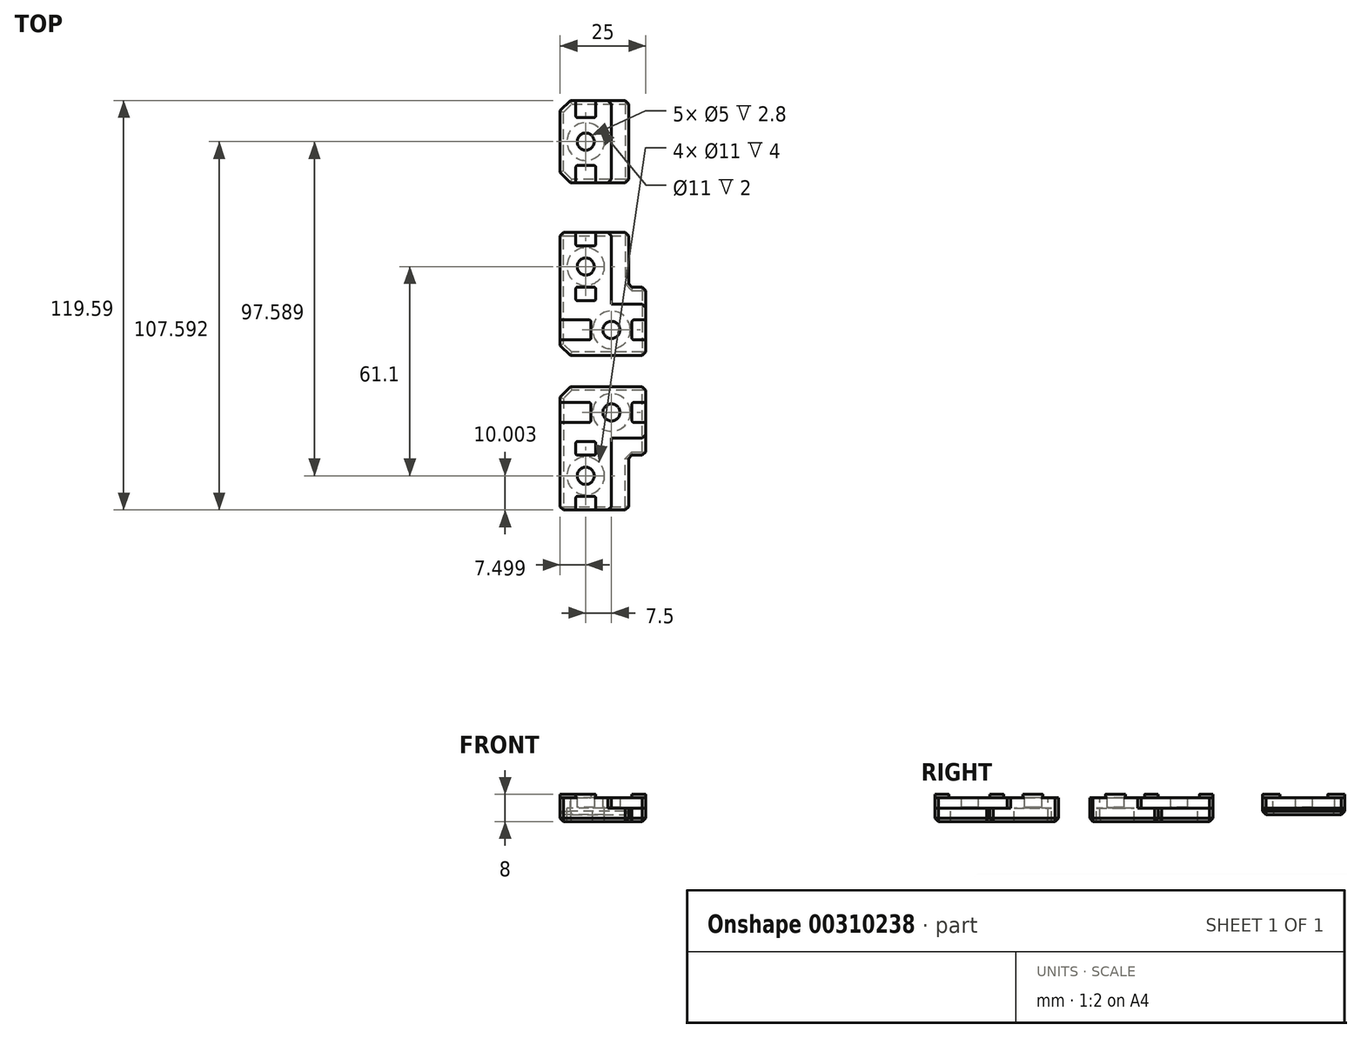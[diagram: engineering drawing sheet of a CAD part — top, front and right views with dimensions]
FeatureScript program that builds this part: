
annotation { "Feature Type Name" : "Feature", "Feature Type Description" : "" }
export const myFeature = defineFeature(function(context is Context, id is Id, definition is map)
    precondition{}
    {
        {
            var Q0;
            Q0=qCreatedBy(makeId("Top.planeOp"),FACE);
            var sketch = newSketch(context, id + "F0", { "sketchPlane" : qUnion([Q0])});
            skLineSegment(sketch, "E0", {"start": v(-211.12, 45.44) * mm, "end": v(-211.12, 81.44) * mm});
            skLineSegment(sketch, "E1", {"start": v(-211.12, 45.44) * mm, "end": v(-186.12, 45.44) * mm});
            skLineSegment(sketch, "E2", {"start": v(-211.12, 81.44) * mm, "end": v(-196.12, 81.44) * mm});
            skLineSegment(sketch, "E3", {"start": v(-196.12, 81.44) * mm, "end": v(-196.12, 60.44) * mm});
            skLineSegment(sketch, "E4", {"start": v(-196.12, 60.44) * mm, "end": v(-186.12, 60.44) * mm});
            skLineSegment(sketch, "E5", {"start": v(-186.12, 60.44) * mm, "end": v(-186.12, 45.44) * mm});
            skCircle(sketch, "E6", {"center": v(-203.62, 71.44) * mm, "radius": 2.5 * mm});
            skPoint(sketch, "E6.centerSnap0", {"position": v(-203.62, 81.44) * mm});
            skCircle(sketch, "E7", {"center": v(-196.12, 52.94) * mm, "radius": 2.5 * mm});
            skPoint(sketch, "E7.centerSnap0", {"position": v(-186.12, 52.94) * mm});
            skLineSegment(sketch, "E8", {"start": v(-191.45, 50.04) * mm, "end": v(-186.12, 50.04) * mm});
            skLineSegment(sketch, "E9", {"start": v(-191.45, 55.84) * mm, "end": v(-186.12, 55.84) * mm});
            skLineSegment(sketch, "E10", {"start": v(-206.52, 76.12) * mm, "end": v(-206.52, 81.44) * mm});
            skLineSegment(sketch, "E11", {"start": v(-200.72, 76.12) * mm, "end": v(-200.72, 81.44) * mm});
            skLineSegment(sketch, "E12", {"start": v(-200.72, 61.44) * mm, "end": v(-200.72, 66.77) * mm});
            skLineSegment(sketch, "E13", {"start": v(-206.52, 66.77) * mm, "end": v(-206.52, 61.44) * mm});
            skCircle(sketch, "E14", {"center": v(-203.62, 71.44) * mm, "radius": 5.5 * mm});
            skCircle(sketch, "E15", {"center": v(-196.12, 52.94) * mm, "radius": 5.5 * mm});
            skLineSegment(sketch, "E16", {"start": v(-200.8, 55.84) * mm, "end": v(-211.12, 55.84) * mm});
            skLineSegment(sketch, "E17", {"start": v(-200.8, 50.04) * mm, "end": v(-211.12, 50.04) * mm});
            skLineSegment(sketch, "E18", {"start": v(-200.72, 61.44) * mm, "end": v(-206.52, 61.44) * mm});
            skLineSegment(sketch, "E19", {"start": v(-206.52, 77.44) * mm, "end": v(-200.72, 77.44) * mm});
            skLineSegment(sketch, "E20", {"start": v(-200.72, 65.44) * mm, "end": v(-206.52, 65.44) * mm});
            skLineSegment(sketch, "E21", {"start": v(-202.12, 55.84) * mm, "end": v(-202.12, 50.04) * mm});
            skLineSegment(sketch, "E22", {"start": v(-190.12, 50.04) * mm, "end": v(-190.12, 55.84) * mm});
            skLineSegment(sketch, "E23", {"start": v(-186.12, 45.44) * mm, "end": v(-183.12, 45.44) * mm});
            skLineSegment(sketch, "E24", {"start": v(-183.12, 45.44) * mm, "end": v(-183.12, 65.44) * mm});
            skLineSegment(sketch, "E25", {"start": v(-183.12, 65.44) * mm, "end": v(-191.12, 65.44) * mm});
            skLineSegment(sketch, "E26", {"start": v(-191.12, 65.44) * mm, "end": v(-191.12, 84.44) * mm});
            skLineSegment(sketch, "E27", {"start": v(-191.12, 84.44) * mm, "end": v(-211.12, 84.44) * mm});
            skLineSegment(sketch, "E28", {"start": v(-211.12, 84.44) * mm, "end": v(-211.12, 81.44) * mm});
            skLineSegment(sketch, "E29", {"start": v(-211.12, 95.93) * mm, "end": v(-196.12, 95.93) * mm});
            skLineSegment(sketch, "E30", {"start": v(-196.12, 95.93) * mm, "end": v(-196.12, 119.93) * mm});
            skLineSegment(sketch, "E31", {"start": v(-196.12, 119.93) * mm, "end": v(-211.12, 119.93) * mm});
            skLineSegment(sketch, "E32", {"start": v(-211.12, 119.93) * mm, "end": v(-211.12, 95.93) * mm});
            skLineSegment(sketch, "E33", {"start": v(-206.52, 95.93) * mm, "end": v(-206.52, 100.93) * mm});
            skLineSegment(sketch, "E34", {"start": v(-206.52, 100.93) * mm, "end": v(-200.72, 100.93) * mm});
            skLineSegment(sketch, "E35", {"start": v(-200.72, 100.93) * mm, "end": v(-200.72, 95.93) * mm});
            skLineSegment(sketch, "E36", {"start": v(-206.52, 119.93) * mm, "end": v(-206.52, 114.93) * mm});
            skLineSegment(sketch, "E37", {"start": v(-206.52, 114.93) * mm, "end": v(-200.72, 114.93) * mm});
            skLineSegment(sketch, "E38", {"start": v(-200.72, 114.93) * mm, "end": v(-200.72, 119.93) * mm});
            skCircle(sketch, "E39", {"center": v(-203.62, 107.93) * mm, "radius": 5.5 * mm});
            skPoint(sketch, "E39.centerSnap0", {"position": v(-196.12, 107.93) * mm});
            skPoint(sketch, "E39.centerSnap1", {"position": v(-203.62, 100.93) * mm});
            skLineSegment(sketch, "E40", {"start": v(-196.12, 119.93) * mm, "end": v(-191.12, 119.93) * mm});
            skLineSegment(sketch, "E41", {"start": v(-191.12, 119.93) * mm, "end": v(-191.12, 95.93) * mm});
            skLineSegment(sketch, "E42", {"start": v(-191.12, 95.93) * mm, "end": v(-196.12, 95.93) * mm});
            skLineSegment(sketch, "E43", {"start": v(-196.12, 81.44) * mm, "end": v(-191.12, 81.44) * mm});
            skLineSegment(sketch, "E44", {"start": v(-186.12, 60.44) * mm, "end": v(-186.12, 65.44) * mm});
            skCircle(sketch, "E45", {"center": v(-203.62, 107.93) * mm, "radius": 2.5 * mm});
            skSolve(sketch);
        }
        {
            var Q0;
            {var subQ9=sQuery(id+"F0.wireOp",EDGE,"E3");Q0=makeQuery(id+"F0.imprint","IMPRINT",FACE,{"disambiguationData":[TD([[makeQuery(id+"F0.imprint","IMPRINT",EDGE,{"derivedFrom":subQ9}),-1.0]])]});}
            var Q1;
            {var subQ0=sQuery(id+"F0.wireOp",EDGE,"E16");Q1=makeQuery(id+"F0.imprint","IMPRINT",FACE,{"disambiguationData":[TD([[makeQuery(id+"F0.imprint","IMPRINT",EDGE,{"derivedFrom":subQ0}),1.0]])]});}
            var Q2;
            {var subQ2=sQuery(id+"F0.wireOp",EDGE,"E1");Q2=makeQuery(id+"F0.imprint","IMPRINT",FACE,{"disambiguationData":[TD([[makeQuery(id+"F0.imprint","IMPRINT",EDGE,{"derivedFrom":subQ2}),1.0]])]});}
            var Q3;
            {var subQ0=sQuery(id+"F0.wireOp",EDGE,"E8");Q3=makeQuery(id+"F0.imprint","IMPRINT",FACE,{"disambiguationData":[TD([[makeQuery(id+"F0.imprint","IMPRINT",EDGE,{"derivedFrom":subQ0}),1.0]])]});}
            var Q4;
            {var subQ0=sQuery(id+"F0.wireOp",EDGE,"E12");Q4=makeQuery(id+"F0.imprint","IMPRINT",FACE,{"disambiguationData":[TD([[makeQuery(id+"F0.imprint","IMPRINT",EDGE,{"derivedFrom":subQ0}),1.0]])]});}
            var Q5;
            {var subQ0=sQuery(id+"F0.wireOp",EDGE,"E10");Q5=makeQuery(id+"F0.imprint","IMPRINT",FACE,{"disambiguationData":[TD([[makeQuery(id+"F0.imprint","IMPRINT",EDGE,{"derivedFrom":subQ0}),-1.0]])]});}
            extrude(context, id + "F1", {"entities" : qUnion([Q0, Q1, Q2, Q3, Q4, Q5]), "oppositeDirection" : true, "depth" : 4 * mm});
        }
        {
            var Q0;
            {var subQ9=sQuery(id+"F0.wireOp",EDGE,"E3");Q0=makeQuery(id+"F0.imprint","IMPRINT",FACE,{"disambiguationData":[TD([[makeQuery(id+"F0.imprint","IMPRINT",EDGE,{"derivedFrom":subQ9}),-1.0]])]});}
            var Q1;
            {var subQ0=sQuery(id+"F0.wireOp",EDGE,"E12");Q1=makeQuery(id+"F0.imprint","IMPRINT",FACE,{"disambiguationData":[TD([[makeQuery(id+"F0.imprint","IMPRINT",EDGE,{"derivedFrom":subQ0}),1.0]])]});}
            var Q2;
            {var subQ0=sQuery(id+"F0.wireOp",EDGE,"E16");Q2=makeQuery(id+"F0.imprint","IMPRINT",FACE,{"disambiguationData":[TD([[makeQuery(id+"F0.imprint","IMPRINT",EDGE,{"derivedFrom":subQ0}),1.0]])]});}
            var Q3;
            {var subQ2=sQuery(id+"F0.wireOp",EDGE,"E1");Q3=makeQuery(id+"F0.imprint","IMPRINT",FACE,{"disambiguationData":[TD([[makeQuery(id+"F0.imprint","IMPRINT",EDGE,{"derivedFrom":subQ2}),1.0]])]});}
            var Q4;
            {var subQ0=sQuery(id+"F0.wireOp",EDGE,"E8");Q4=makeQuery(id+"F0.imprint","IMPRINT",FACE,{"disambiguationData":[TD([[makeQuery(id+"F0.imprint","IMPRINT",EDGE,{"derivedFrom":subQ0}),1.0]])]});}
            var Q5;
            Q5=makeQuery(id+"F0.imprint","IMPRINT",FACE,{"disambiguationData":[TD([[makeQuery(id+"F0.imprint","IMPRINT",EDGE,{"derivedFrom":sQuery(id+"F0.wireOp",EDGE,"E6")}),-1.0]])]});
            var Q6;
            {var subQ0=sQuery(id+"F0.wireOp",EDGE,"E10");Q6=makeQuery(id+"F0.imprint","IMPRINT",FACE,{"disambiguationData":[TD([[makeQuery(id+"F0.imprint","IMPRINT",EDGE,{"derivedFrom":subQ0}),-1.0]])]});}
            var Q7;
            Q7=makeQuery(id+"F0.imprint","IMPRINT",FACE,{"disambiguationData":[TD([[makeQuery(id+"F0.imprint","IMPRINT",EDGE,{"derivedFrom":sQuery(id+"F0.wireOp",EDGE,"E7")}),-1.0]])]});
            var Q8;
            {var subQ2=sQuery(id+"F0.wireOp",EDGE,"E30");Q8=makeQuery(id+"F0.imprint","IMPRINT",FACE,{"disambiguationData":[TD([[makeQuery(id+"F0.imprint","IMPRINT",EDGE,{"derivedFrom":subQ2}),1.0]])]});}
            var Q9;
            {var subQ0=sQuery(id+"F0.wireOp",EDGE,"E33");Q9=makeQuery(id+"F0.imprint","IMPRINT",FACE,{"disambiguationData":[TD([[makeQuery(id+"F0.imprint","IMPRINT",EDGE,{"derivedFrom":subQ0}),-1.0]])]});}
            var Q10;
            {var subQ0=sQuery(id+"F0.wireOp",EDGE,"E36");Q10=makeQuery(id+"F0.imprint","IMPRINT",FACE,{"disambiguationData":[TD([[makeQuery(id+"F0.imprint","IMPRINT",EDGE,{"derivedFrom":subQ0}),1.0]])]});}
            var Q11;
            Q11=makeQuery(id+"F0.imprint","IMPRINT",FACE,{"disambiguationData":[TD([[makeQuery(id+"F0.imprint","IMPRINT",EDGE,{"derivedFrom":sQuery(id+"F0.wireOp",EDGE,"E39")}),1.0]])]});
            extrude(context, id + "F2", {"entities" : qUnion([Q0, Q1, Q2, Q3, Q4, Q5, Q6, Q7, Q8, Q9, Q10, Q11]), "operationType" : NewBodyOperationType.ADD, "depth" : 3 * mm});
        }
        {
            var Q0;
            {var subQ0=sQuery(id+"F0.wireOp",EDGE,"E18");Q0=makeQuery(id+"F0.imprint","IMPRINT",FACE,{"disambiguationData":[TD([[makeQuery(id+"F0.imprint","IMPRINT",EDGE,{"derivedFrom":subQ0}),-1.0]])]});}
            var Q1;
            {var subQ5=sQuery(id+"F0.wireOp",EDGE,"E19");Q1=makeQuery(id+"F0.imprint","IMPRINT",FACE,{"disambiguationData":[TD([[makeQuery(id+"F0.imprint","IMPRINT",EDGE,{"derivedFrom":subQ5}),1.0]])]});}
            var Q2;
            {var subQ5=sQuery(id+"F0.wireOp",EDGE,"E21");Q2=makeQuery(id+"F0.imprint","IMPRINT",FACE,{"disambiguationData":[TD([[makeQuery(id+"F0.imprint","IMPRINT",EDGE,{"derivedFrom":subQ5}),-1.0]])]});}
            var Q3;
            {var subQ5=sQuery(id+"F0.wireOp",EDGE,"E22");Q3=makeQuery(id+"F0.imprint","IMPRINT",FACE,{"disambiguationData":[TD([[makeQuery(id+"F0.imprint","IMPRINT",EDGE,{"derivedFrom":subQ5}),-1.0]])]});}
            var Q4;
            {var subQ0=sQuery(id+"F0.wireOp",EDGE,"E33");Q4=makeQuery(id+"F0.imprint","IMPRINT",FACE,{"disambiguationData":[TD([[makeQuery(id+"F0.imprint","IMPRINT",EDGE,{"derivedFrom":subQ0}),-1.0]])]});}
            var Q5;
            {var subQ0=sQuery(id+"F0.wireOp",EDGE,"E36");Q5=makeQuery(id+"F0.imprint","IMPRINT",FACE,{"disambiguationData":[TD([[makeQuery(id+"F0.imprint","IMPRINT",EDGE,{"derivedFrom":subQ0}),1.0]])]});}
            extrude(context, id + "F3", {"entities" : qUnion([Q0, Q1, Q2, Q3, Q4, Q5]), "operationType" : NewBodyOperationType.ADD, "depth" : 4 * mm});
        }
        {
            var Q0;
            {var subQ9=sQuery(id+"F0.wireOp",EDGE,"E3");Q0=makeQuery(id+"F0.imprint","IMPRINT",FACE,{"disambiguationData":[TD([[makeQuery(id+"F0.imprint","IMPRINT",EDGE,{"derivedFrom":subQ9}),1.0]])]});}
            extrude(context, id + "F4", {"entities" : qUnion([Q0]), "operationType" : NewBodyOperationType.ADD, "oppositeDirection" : true, "depth" : 4 * mm});
        }
        {
            var Q0;
            {var subQ2=sQuery(id+"F0.wireOp",EDGE,"E30");Q0=makeQuery(id+"F0.imprint","IMPRINT",FACE,{"disambiguationData":[TD([[makeQuery(id+"F0.imprint","IMPRINT",EDGE,{"derivedFrom":subQ2}),1.0]])]});}
            var Q1;
            Q1=makeQuery(id+"F0.imprint","IMPRINT",FACE,{"disambiguationData":[TD([[makeQuery(id+"F0.imprint","IMPRINT",EDGE,{"derivedFrom":sQuery(id+"F0.wireOp",EDGE,"E30")}),-1.0]])]});
            var Q2;
            {var subQ0=sQuery(id+"F0.wireOp",EDGE,"E33");Q2=makeQuery(id+"F0.imprint","IMPRINT",FACE,{"disambiguationData":[TD([[makeQuery(id+"F0.imprint","IMPRINT",EDGE,{"derivedFrom":subQ0}),-1.0]])]});}
            var Q3;
            {var subQ0=sQuery(id+"F0.wireOp",EDGE,"E36");Q3=makeQuery(id+"F0.imprint","IMPRINT",FACE,{"disambiguationData":[TD([[makeQuery(id+"F0.imprint","IMPRINT",EDGE,{"derivedFrom":subQ0}),1.0]])]});}
            extrude(context, id + "F5", {"entities" : qUnion([Q0, Q1, Q2, Q3]), "operationType" : NewBodyOperationType.ADD, "oppositeDirection" : true, "depth" : 2 * mm});
        }
        {
            var Q0;
            {var subQ0=sQuery(id+"F0.wireOp",EDGE,"E1");var subQ1=sQuery(id+"F0.wireOp",EDGE,"E0");Q0=makeQuery(id+"F2.boolean.opBoolean","MERGE",EDGE,{"derivedFrom":[makeQuery(id+"F1.opExtrude","SWEPT_EDGE",EDGE,{"disambiguationData":[OSD([subQ1,subQ0])]}),makeQuery(id+"F2.opExtrude","SWEPT_EDGE",EDGE,{"disambiguationData":[OSD([subQ1,subQ0])]})]});}
            var Q1;
            {var subQ0=sQuery(id+"F0.wireOp",EDGE,"E32");var subQ1=sQuery(id+"F0.wireOp",EDGE,"E29");Q1=makeQuery(id+"F5.boolean.opBoolean","MERGE",EDGE,{"derivedFrom":[makeQuery(id+"F2.opExtrude","SWEPT_EDGE",EDGE,{"disambiguationData":[OSD([subQ1,subQ0])]}),makeQuery(id+"F5.opExtrude","SWEPT_EDGE",EDGE,{"disambiguationData":[OSD([subQ1,subQ0])]})]});}
            var Q2;
            {var subQ0=sQuery(id+"F0.wireOp",EDGE,"E32");var subQ1=sQuery(id+"F0.wireOp",EDGE,"E31");Q2=makeQuery(id+"F5.boolean.opBoolean","MERGE",EDGE,{"derivedFrom":[makeQuery(id+"F2.opExtrude","SWEPT_EDGE",EDGE,{"disambiguationData":[OSD([subQ1,subQ0])]}),makeQuery(id+"F5.opExtrude","SWEPT_EDGE",EDGE,{"disambiguationData":[OSD([subQ1,subQ0])]})]});}
            chamfer(context, id + "F6", {"entities" : qUnion([Q0, Q1, Q2]), "width" : 3 * mm, "tangentPropagation" : true});
        }
        {
            var Q0;
            {var subQ0=sQuery(id+"F0.wireOp",EDGE,"E23");var subQ1=sQuery(id+"F0.wireOp",EDGE,"E5");var subQ2=sQuery(id+"F0.wireOp",EDGE,"E1");Q0=makeQuery(id+"F2.boolean.opBoolean","MERGE",EDGE,{"derivedFrom":[makeQuery(id+"F1.opExtrude","SWEPT_EDGE",EDGE,{"disambiguationData":[OSD([subQ2,subQ1,subQ0])]}),makeQuery(id+"F2.opExtrude","SWEPT_EDGE",EDGE,{"disambiguationData":[OSD([subQ2,subQ1,subQ0])]})]});}
            var Q1;
            {var subQ0=sQuery(id+"F0.wireOp",EDGE,"E3");var subQ1=sQuery(id+"F0.wireOp",EDGE,"E2");Q1=makeQuery(id+"F2.boolean.opBoolean","MERGE",EDGE,{"derivedFrom":[makeQuery(id+"F1.opExtrude","SWEPT_EDGE",EDGE,{"disambiguationData":[OSD([subQ1,subQ0])]}),makeQuery(id+"F2.opExtrude","SWEPT_EDGE",EDGE,{"disambiguationData":[OSD([subQ1,subQ0])]})]});}
            var Q2;
            Q2=makeQuery(id+"F4.boolean.opBoolean","MERGE",EDGE,{"derivedFrom":[makeQuery(id+"F1.opExtrude","CAP_EDGE",EDGE,{"disambiguationData":[OSD([sQuery(id+"F0.wireOp",EDGE,"E1")])],"isStart":false}),makeQuery(id+"F4.opExtrude","CAP_EDGE",EDGE,{"disambiguationData":[OSD([sQuery(id+"F0.wireOp",EDGE,"E23")])],"isStart":false})]});
            var Q3;
            {var subQ0=sQuery(id+"F0.wireOp",EDGE,"E5");var subQ1=sQuery(id+"F0.wireOp",EDGE,"E4");var subQ2=sQuery(id+"F0.wireOp",EDGE,"E3");var subQ3=sQuery(id+"F0.wireOp",EDGE,"E2");var subQ4=sQuery(id+"F0.wireOp",EDGE,"E1");var subQ5=sQuery(id+"F0.wireOp",EDGE,"E0");Q3=makeQuery(id+"F6.opChamfer","BLEND_EDGE",EDGE,{"blendedFrom":[makeQuery(id+"F2.boolean.opBoolean","MERGE",EDGE,{"derivedFrom":[makeQuery(id+"F1.opExtrude","SWEPT_EDGE",EDGE,{"disambiguationData":[OSD([subQ5,subQ4])]}),makeQuery(id+"F2.opExtrude","SWEPT_EDGE",EDGE,{"disambiguationData":[OSD([subQ5,subQ4])]})]}),makeQuery(id+"F4.boolean.opBoolean","MERGE",FACE,{"derivedFrom":[makeQuery(id+"F1.opExtrude","CAP_FACE",FACE,{"disambiguationData":[OSD([subQ5,subQ4,subQ3,subQ2,subQ1,subQ0,sQuery(id+"F0.wireOp",EDGE,"E14"),sQuery(id+"F0.wireOp",EDGE,"E15")])],"isStart":false}),makeQuery(id+"F4.opExtrude","CAP_FACE",FACE,{"disambiguationData":[OSD([subQ3,subQ2,subQ1,subQ0,sQuery(id+"F0.wireOp",EDGE,"E23"),sQuery(id+"F0.wireOp",EDGE,"E24"),sQuery(id+"F0.wireOp",EDGE,"E25"),sQuery(id+"F0.wireOp",EDGE,"E26"),sQuery(id+"F0.wireOp",EDGE,"E27"),sQuery(id+"F0.wireOp",EDGE,"E28")])],"isStart":false})]})],"blendedInto":[makeQuery(id+"F4.boolean.opBoolean","MERGE",FACE,{"derivedFrom":[makeQuery(id+"F1.opExtrude","CAP_FACE",FACE,{"disambiguationData":[OSD([subQ5,subQ4,subQ3,subQ2,subQ1,subQ0,sQuery(id+"F0.wireOp",EDGE,"E14"),sQuery(id+"F0.wireOp",EDGE,"E15")])],"isStart":false}),makeQuery(id+"F4.opExtrude","CAP_FACE",FACE,{"disambiguationData":[OSD([subQ3,subQ2,subQ1,subQ0,sQuery(id+"F0.wireOp",EDGE,"E23"),sQuery(id+"F0.wireOp",EDGE,"E24"),sQuery(id+"F0.wireOp",EDGE,"E25"),sQuery(id+"F0.wireOp",EDGE,"E26"),sQuery(id+"F0.wireOp",EDGE,"E27"),sQuery(id+"F0.wireOp",EDGE,"E28")])],"isStart":false})]})]});}
            var Q4;
            Q4=makeQuery(id+"F4.boolean.opBoolean","MERGE",EDGE,{"derivedFrom":[makeQuery(id+"F1.opExtrude","CAP_EDGE",EDGE,{"disambiguationData":[OSD([sQuery(id+"F0.wireOp",EDGE,"E0")])],"isStart":false}),makeQuery(id+"F4.opExtrude","CAP_EDGE",EDGE,{"disambiguationData":[OSD([sQuery(id+"F0.wireOp",EDGE,"E28")])],"isStart":false})]});
            var Q5;
            {var subQ0=sQuery(id+"F0.wireOp",EDGE,"E28");var subQ1=sQuery(id+"F0.wireOp",EDGE,"E27");var subQ2=sQuery(id+"F0.wireOp",EDGE,"E5");var subQ3=sQuery(id+"F0.wireOp",EDGE,"E4");var subQ4=sQuery(id+"F0.wireOp",EDGE,"E3");var subQ5=sQuery(id+"F0.wireOp",EDGE,"E2");Q5=makeQuery(id+"F6.opChamfer","BLEND_EDGE",EDGE,{"blendedFrom":[makeQuery(id+"F4.opExtrude","SWEPT_EDGE",EDGE,{"disambiguationData":[OSD([subQ1,subQ0])]}),makeQuery(id+"F4.boolean.opBoolean","MERGE",FACE,{"derivedFrom":[makeQuery(id+"F1.opExtrude","CAP_FACE",FACE,{"disambiguationData":[OSD([sQuery(id+"F0.wireOp",EDGE,"E0"),sQuery(id+"F0.wireOp",EDGE,"E1"),subQ5,subQ4,subQ3,subQ2,sQuery(id+"F0.wireOp",EDGE,"E14"),sQuery(id+"F0.wireOp",EDGE,"E15")])],"isStart":false}),makeQuery(id+"F4.opExtrude","CAP_FACE",FACE,{"disambiguationData":[OSD([subQ5,subQ4,subQ3,subQ2,sQuery(id+"F0.wireOp",EDGE,"E23"),sQuery(id+"F0.wireOp",EDGE,"E24"),sQuery(id+"F0.wireOp",EDGE,"E25"),sQuery(id+"F0.wireOp",EDGE,"E26"),subQ1,subQ0])],"isStart":false})]})],"blendedInto":[makeQuery(id+"F4.boolean.opBoolean","MERGE",FACE,{"derivedFrom":[makeQuery(id+"F1.opExtrude","CAP_FACE",FACE,{"disambiguationData":[OSD([sQuery(id+"F0.wireOp",EDGE,"E0"),sQuery(id+"F0.wireOp",EDGE,"E1"),subQ5,subQ4,subQ3,subQ2,sQuery(id+"F0.wireOp",EDGE,"E14"),sQuery(id+"F0.wireOp",EDGE,"E15")])],"isStart":false}),makeQuery(id+"F4.opExtrude","CAP_FACE",FACE,{"disambiguationData":[OSD([subQ5,subQ4,subQ3,subQ2,sQuery(id+"F0.wireOp",EDGE,"E23"),sQuery(id+"F0.wireOp",EDGE,"E24"),sQuery(id+"F0.wireOp",EDGE,"E25"),sQuery(id+"F0.wireOp",EDGE,"E26"),subQ1,subQ0])],"isStart":false})]})]});}
            var Q6;
            {var subQ0=sQuery(id+"F0.wireOp",EDGE,"E24");var subQ1=sQuery(id+"F0.wireOp",EDGE,"E23");var subQ2=sQuery(id+"F0.wireOp",EDGE,"E5");var subQ3=sQuery(id+"F0.wireOp",EDGE,"E4");var subQ4=sQuery(id+"F0.wireOp",EDGE,"E3");var subQ5=sQuery(id+"F0.wireOp",EDGE,"E2");Q6=makeQuery(id+"F6.opChamfer","BLEND_EDGE",EDGE,{"blendedFrom":[makeQuery(id+"F4.opExtrude","SWEPT_EDGE",EDGE,{"disambiguationData":[OSD([subQ1,subQ0])]}),makeQuery(id+"F4.boolean.opBoolean","MERGE",FACE,{"derivedFrom":[makeQuery(id+"F1.opExtrude","CAP_FACE",FACE,{"disambiguationData":[OSD([sQuery(id+"F0.wireOp",EDGE,"E0"),sQuery(id+"F0.wireOp",EDGE,"E1"),subQ5,subQ4,subQ3,subQ2,sQuery(id+"F0.wireOp",EDGE,"E14"),sQuery(id+"F0.wireOp",EDGE,"E15")])],"isStart":false}),makeQuery(id+"F4.opExtrude","CAP_FACE",FACE,{"disambiguationData":[OSD([subQ5,subQ4,subQ3,subQ2,subQ1,subQ0,sQuery(id+"F0.wireOp",EDGE,"E25"),sQuery(id+"F0.wireOp",EDGE,"E26"),sQuery(id+"F0.wireOp",EDGE,"E27"),sQuery(id+"F0.wireOp",EDGE,"E28")])],"isStart":false})]})],"blendedInto":[makeQuery(id+"F4.boolean.opBoolean","MERGE",FACE,{"derivedFrom":[makeQuery(id+"F1.opExtrude","CAP_FACE",FACE,{"disambiguationData":[OSD([sQuery(id+"F0.wireOp",EDGE,"E0"),sQuery(id+"F0.wireOp",EDGE,"E1"),subQ5,subQ4,subQ3,subQ2,sQuery(id+"F0.wireOp",EDGE,"E14"),sQuery(id+"F0.wireOp",EDGE,"E15")])],"isStart":false}),makeQuery(id+"F4.opExtrude","CAP_FACE",FACE,{"disambiguationData":[OSD([subQ5,subQ4,subQ3,subQ2,subQ1,subQ0,sQuery(id+"F0.wireOp",EDGE,"E25"),sQuery(id+"F0.wireOp",EDGE,"E26"),sQuery(id+"F0.wireOp",EDGE,"E27"),sQuery(id+"F0.wireOp",EDGE,"E28")])],"isStart":false})]})]});}
            var Q7;
            {var subQ0=sQuery(id+"F0.wireOp",EDGE,"E5");var subQ1=sQuery(id+"F0.wireOp",EDGE,"E4");Q7=makeQuery(id+"F2.boolean.opBoolean","MERGE",EDGE,{"derivedFrom":[makeQuery(id+"F1.opExtrude","SWEPT_EDGE",EDGE,{"disambiguationData":[OSD([subQ1,subQ0])]}),makeQuery(id+"F2.opExtrude","SWEPT_EDGE",EDGE,{"disambiguationData":[OSD([subQ1,subQ0])]})]});}
            var Q8;
            {var subQ0=sQuery(id+"F0.wireOp",EDGE,"E28");var subQ1=sQuery(id+"F0.wireOp",EDGE,"E2");var subQ2=sQuery(id+"F0.wireOp",EDGE,"E0");Q8=makeQuery(id+"F2.boolean.opBoolean","MERGE",EDGE,{"derivedFrom":[makeQuery(id+"F1.opExtrude","SWEPT_EDGE",EDGE,{"disambiguationData":[OSD([subQ2,subQ1,subQ0])]}),makeQuery(id+"F2.opExtrude","SWEPT_EDGE",EDGE,{"disambiguationData":[OSD([subQ2,subQ1,subQ0])]})]});}
            var Q9;
            Q9=makeQuery(id+"F4.opExtrude","SWEPT_EDGE",EDGE,{"disambiguationData":[OSD([sQuery(id+"F0.wireOp",EDGE,"E25"),sQuery(id+"F0.wireOp",EDGE,"E26")])]});
            var Q10;
            Q10=makeQuery(id+"F4.opExtrude","SWEPT_EDGE",EDGE,{"disambiguationData":[OSD([sQuery(id+"F0.wireOp",EDGE,"E23"),sQuery(id+"F0.wireOp",EDGE,"E24")])]});
            var Q11;
            Q11=makeQuery(id+"F4.opExtrude","SWEPT_EDGE",EDGE,{"disambiguationData":[OSD([sQuery(id+"F0.wireOp",EDGE,"E24"),sQuery(id+"F0.wireOp",EDGE,"E25")])]});
            var Q12;
            Q12=makeQuery(id+"F4.opExtrude","SWEPT_EDGE",EDGE,{"disambiguationData":[OSD([sQuery(id+"F0.wireOp",EDGE,"E26"),sQuery(id+"F0.wireOp",EDGE,"E27")])]});
            var Q13;
            Q13=makeQuery(id+"F4.opExtrude","SWEPT_EDGE",EDGE,{"disambiguationData":[OSD([sQuery(id+"F0.wireOp",EDGE,"E27"),sQuery(id+"F0.wireOp",EDGE,"E28")])]});
            var Q14;
            Q14=makeQuery(id+"F4.opExtrude","CAP_EDGE",EDGE,{"disambiguationData":[OSD([sQuery(id+"F0.wireOp",EDGE,"E27")])],"isStart":false});
            var Q15;
            Q15=makeQuery(id+"F4.opExtrude","CAP_EDGE",EDGE,{"disambiguationData":[OSD([sQuery(id+"F0.wireOp",EDGE,"E26")])],"isStart":false});
            var Q16;
            Q16=makeQuery(id+"F4.opExtrude","CAP_EDGE",EDGE,{"disambiguationData":[OSD([sQuery(id+"F0.wireOp",EDGE,"E24")])],"isStart":false});
            var Q17;
            Q17=makeQuery(id+"F4.opExtrude","CAP_EDGE",EDGE,{"disambiguationData":[OSD([sQuery(id+"F0.wireOp",EDGE,"E25")])],"isStart":false});
            var Q18;
            Q18=makeQuery(id+"F2.opExtrude","SWEPT_EDGE",EDGE,{"disambiguationData":[OSD([sQuery(id+"F0.wireOp",EDGE,"E29"),sQuery(id+"F0.wireOp",EDGE,"E30"),sQuery(id+"F0.wireOp",EDGE,"E42")])]});
            var Q19;
            Q19=makeQuery(id+"F2.opExtrude","SWEPT_EDGE",EDGE,{"disambiguationData":[OSD([sQuery(id+"F0.wireOp",EDGE,"E30"),sQuery(id+"F0.wireOp",EDGE,"E31"),sQuery(id+"F0.wireOp",EDGE,"E40")])]});
            var Q20;
            Q20=makeQuery(id+"F5.opExtrude","SWEPT_EDGE",EDGE,{"disambiguationData":[OSD([sQuery(id+"F0.wireOp",EDGE,"E40"),sQuery(id+"F0.wireOp",EDGE,"E41")])]});
            var Q21;
            Q21=makeQuery(id+"F5.opExtrude","SWEPT_EDGE",EDGE,{"disambiguationData":[OSD([sQuery(id+"F0.wireOp",EDGE,"E41"),sQuery(id+"F0.wireOp",EDGE,"E42")])]});
            var Q22;
            Q22=makeQuery(id+"F4.boolean.opBoolean","MERGE",EDGE,{"derivedFrom":[makeQuery(id+"F1.opExtrude","CAP_EDGE",EDGE,{"disambiguationData":[OSD([sQuery(id+"F0.wireOp",EDGE,"E2")])],"isStart":false}),makeQuery(id+"F4.opExtrude","CAP_EDGE",EDGE,{"disambiguationData":[OSD([sQuery(id+"F0.wireOp",EDGE,"E43")])],"isStart":false})]});
            var Q23;
            Q23=makeQuery(id+"F1.opExtrude","CAP_EDGE",EDGE,{"disambiguationData":[OSD([sQuery(id+"F0.wireOp",EDGE,"E0")])],"isStart":false});
            var Q24;
            Q24=makeQuery(id+"F1.opExtrude","CAP_EDGE",EDGE,{"disambiguationData":[OSD([sQuery(id+"F0.wireOp",EDGE,"E1")])],"isStart":false});
            var Q25;
            Q25=makeQuery(id+"F4.boolean.opBoolean","MERGE",EDGE,{"derivedFrom":[makeQuery(id+"F1.opExtrude","CAP_EDGE",EDGE,{"disambiguationData":[OSD([sQuery(id+"F0.wireOp",EDGE,"E5")])],"isStart":false}),makeQuery(id+"F4.opExtrude","CAP_EDGE",EDGE,{"disambiguationData":[OSD([sQuery(id+"F0.wireOp",EDGE,"E44")])],"isStart":false})]});
            var Q26;
            Q26=makeQuery(id+"F5.opExtrude","CAP_EDGE",EDGE,{"disambiguationData":[OSD([sQuery(id+"F0.wireOp",EDGE,"E41")])],"isStart":false});
            var Q27;
            Q27=makeQuery(id+"F5.opExtrude","CAP_EDGE",EDGE,{"disambiguationData":[OSD([sQuery(id+"F0.wireOp",EDGE,"E31"),sQuery(id+"F0.wireOp",EDGE,"E40")])],"isStart":false});
            var Q28;
            Q28=makeQuery(id+"F5.opExtrude","CAP_EDGE",EDGE,{"disambiguationData":[OSD([sQuery(id+"F0.wireOp",EDGE,"E32")])],"isStart":false});
            var Q29;
            {var subQ0=sQuery(id+"F0.wireOp",EDGE,"E32");var subQ1=sQuery(id+"F0.wireOp",EDGE,"E31");Q29=makeQuery(id+"F6.opChamfer","BLEND_EDGE",EDGE,{"blendedFrom":[makeQuery(id+"F5.boolean.opBoolean","MERGE",EDGE,{"derivedFrom":[makeQuery(id+"F2.opExtrude","SWEPT_EDGE",EDGE,{"disambiguationData":[OSD([subQ1,subQ0])]}),makeQuery(id+"F5.opExtrude","SWEPT_EDGE",EDGE,{"disambiguationData":[OSD([subQ1,subQ0])]})]}),makeQuery(id+"F5.opExtrude","CAP_FACE",FACE,{"disambiguationData":[OSD([sQuery(id+"F0.wireOp",EDGE,"E29"),subQ1,subQ0,sQuery(id+"F0.wireOp",EDGE,"E39"),sQuery(id+"F0.wireOp",EDGE,"E40"),sQuery(id+"F0.wireOp",EDGE,"E41"),sQuery(id+"F0.wireOp",EDGE,"E42")])],"isStart":false})],"blendedInto":[makeQuery(id+"F5.opExtrude","CAP_FACE",FACE,{"disambiguationData":[OSD([sQuery(id+"F0.wireOp",EDGE,"E29"),subQ1,subQ0,sQuery(id+"F0.wireOp",EDGE,"E39"),sQuery(id+"F0.wireOp",EDGE,"E40"),sQuery(id+"F0.wireOp",EDGE,"E41"),sQuery(id+"F0.wireOp",EDGE,"E42")])],"isStart":false})]});}
            var Q30;
            {var subQ0=sQuery(id+"F0.wireOp",EDGE,"E32");var subQ1=sQuery(id+"F0.wireOp",EDGE,"E29");Q30=makeQuery(id+"F6.opChamfer","BLEND_EDGE",EDGE,{"blendedFrom":[makeQuery(id+"F5.boolean.opBoolean","MERGE",EDGE,{"derivedFrom":[makeQuery(id+"F2.opExtrude","SWEPT_EDGE",EDGE,{"disambiguationData":[OSD([subQ1,subQ0])]}),makeQuery(id+"F5.opExtrude","SWEPT_EDGE",EDGE,{"disambiguationData":[OSD([subQ1,subQ0])]})]}),makeQuery(id+"F5.opExtrude","CAP_FACE",FACE,{"disambiguationData":[OSD([subQ1,sQuery(id+"F0.wireOp",EDGE,"E31"),subQ0,sQuery(id+"F0.wireOp",EDGE,"E39"),sQuery(id+"F0.wireOp",EDGE,"E40"),sQuery(id+"F0.wireOp",EDGE,"E41"),sQuery(id+"F0.wireOp",EDGE,"E42")])],"isStart":false})],"blendedInto":[makeQuery(id+"F5.opExtrude","CAP_FACE",FACE,{"disambiguationData":[OSD([subQ1,sQuery(id+"F0.wireOp",EDGE,"E31"),subQ0,sQuery(id+"F0.wireOp",EDGE,"E39"),sQuery(id+"F0.wireOp",EDGE,"E40"),sQuery(id+"F0.wireOp",EDGE,"E41"),sQuery(id+"F0.wireOp",EDGE,"E42")])],"isStart":false})]});}
            var Q31;
            Q31=makeQuery(id+"F5.opExtrude","CAP_EDGE",EDGE,{"disambiguationData":[OSD([sQuery(id+"F0.wireOp",EDGE,"E29"),sQuery(id+"F0.wireOp",EDGE,"E42")])],"isStart":false});
            chamfer(context, id + "F7", {"entities" : qUnion([Q0, Q1, Q2, Q3, Q4, Q5, Q6, Q7, Q8, Q9, Q10, Q11, Q12, Q13, Q14, Q15, Q16, Q17, Q18, Q19, Q20, Q21, Q22, Q23, Q24, Q25, Q26, Q27, Q28, Q29, Q30, Q31]), "width" : 1 * mm, "tangentPropagation" : true});
        }
        {
            var Q0;
            Q0=makeQuery(id+"F0.imprint","IMPRINT",FACE,{"disambiguationData":[TD([[makeQuery(id+"F0.imprint","IMPRINT",EDGE,{"derivedFrom":sQuery(id+"F0.wireOp",EDGE,"E6")}),1.0]])]});
            var Q1;
            Q1=makeQuery(id+"F0.imprint","IMPRINT",FACE,{"disambiguationData":[TD([[makeQuery(id+"F0.imprint","IMPRINT",EDGE,{"derivedFrom":sQuery(id+"F0.wireOp",EDGE,"E7")}),1.0]])]});
            var Q2;
            Q2=makeQuery(id+"F0.imprint","IMPRINT",FACE,{"disambiguationData":[TD([[makeQuery(id+"F0.imprint","IMPRINT",EDGE,{"derivedFrom":sQuery(id+"F0.wireOp",EDGE,"E45")}),1.0]])]});
            extrude(context, id + "F8", {"entities" : qUnion([Q0, Q1, Q2]), "operationType" : NewBodyOperationType.ADD, "depth" : .2 * mm});
        }
        {
            var Q0;
            Q0=makeQuery(id+"F3.opExtrude","SWEPT_EDGE",EDGE,{"disambiguationData":[OSD([sQuery(id+"F0.wireOp",EDGE,"E5"),sQuery(id+"F0.wireOp",EDGE,"E9")])]});
            var Q1;
            Q1=makeQuery(id+"F3.opExtrude","SWEPT_EDGE",EDGE,{"disambiguationData":[OSD([sQuery(id+"F0.wireOp",EDGE,"E9"),sQuery(id+"F0.wireOp",EDGE,"E22")])]});
            var Q2;
            Q2=makeQuery(id+"F3.opExtrude","SWEPT_EDGE",EDGE,{"disambiguationData":[OSD([sQuery(id+"F0.wireOp",EDGE,"E5"),sQuery(id+"F0.wireOp",EDGE,"E8")])]});
            var Q3;
            Q3=makeQuery(id+"F3.opExtrude","SWEPT_EDGE",EDGE,{"disambiguationData":[OSD([sQuery(id+"F0.wireOp",EDGE,"E8"),sQuery(id+"F0.wireOp",EDGE,"E22")])]});
            var Q4;
            Q4=makeQuery(id+"F3.opExtrude","SWEPT_EDGE",EDGE,{"disambiguationData":[OSD([sQuery(id+"F0.wireOp",EDGE,"E12"),sQuery(id+"F0.wireOp",EDGE,"E18")])]});
            var Q5;
            Q5=makeQuery(id+"F3.opExtrude","SWEPT_EDGE",EDGE,{"disambiguationData":[OSD([sQuery(id+"F0.wireOp",EDGE,"E13"),sQuery(id+"F0.wireOp",EDGE,"E18")])]});
            var Q6;
            Q6=makeQuery(id+"F3.opExtrude","SWEPT_EDGE",EDGE,{"disambiguationData":[OSD([sQuery(id+"F0.wireOp",EDGE,"E13"),sQuery(id+"F0.wireOp",EDGE,"E20")])]});
            var Q7;
            Q7=makeQuery(id+"F3.opExtrude","SWEPT_EDGE",EDGE,{"disambiguationData":[OSD([sQuery(id+"F0.wireOp",EDGE,"E12"),sQuery(id+"F0.wireOp",EDGE,"E20")])]});
            var Q8;
            Q8=makeQuery(id+"F3.opExtrude","SWEPT_EDGE",EDGE,{"disambiguationData":[OSD([sQuery(id+"F0.wireOp",EDGE,"E2"),sQuery(id+"F0.wireOp",EDGE,"E11")])]});
            var Q9;
            Q9=makeQuery(id+"F3.opExtrude","SWEPT_EDGE",EDGE,{"disambiguationData":[OSD([sQuery(id+"F0.wireOp",EDGE,"E2"),sQuery(id+"F0.wireOp",EDGE,"E10")])]});
            var Q10;
            Q10=makeQuery(id+"F3.opExtrude","SWEPT_EDGE",EDGE,{"disambiguationData":[OSD([sQuery(id+"F0.wireOp",EDGE,"E10"),sQuery(id+"F0.wireOp",EDGE,"E19")])]});
            var Q11;
            Q11=makeQuery(id+"F3.opExtrude","SWEPT_EDGE",EDGE,{"disambiguationData":[OSD([sQuery(id+"F0.wireOp",EDGE,"E11"),sQuery(id+"F0.wireOp",EDGE,"E19")])]});
            var Q12;
            Q12=makeQuery(id+"F3.opExtrude","SWEPT_EDGE",EDGE,{"disambiguationData":[OSD([sQuery(id+"F0.wireOp",EDGE,"E17"),sQuery(id+"F0.wireOp",EDGE,"E21")])]});
            var Q13;
            Q13=makeQuery(id+"F3.opExtrude","SWEPT_EDGE",EDGE,{"disambiguationData":[OSD([sQuery(id+"F0.wireOp",EDGE,"E16"),sQuery(id+"F0.wireOp",EDGE,"E21")])]});
            var Q14;
            Q14=makeQuery(id+"F3.opExtrude","SWEPT_EDGE",EDGE,{"disambiguationData":[OSD([sQuery(id+"F0.wireOp",EDGE,"E0"),sQuery(id+"F0.wireOp",EDGE,"E17")])]});
            var Q15;
            Q15=makeQuery(id+"F3.opExtrude","SWEPT_EDGE",EDGE,{"disambiguationData":[OSD([sQuery(id+"F0.wireOp",EDGE,"E0"),sQuery(id+"F0.wireOp",EDGE,"E16")])]});
            var Q16;
            Q16=makeQuery(id+"F3.opExtrude","SWEPT_EDGE",EDGE,{"disambiguationData":[OSD([sQuery(id+"F0.wireOp",EDGE,"E29"),sQuery(id+"F0.wireOp",EDGE,"E33")])]});
            var Q17;
            Q17=makeQuery(id+"F3.opExtrude","SWEPT_EDGE",EDGE,{"disambiguationData":[OSD([sQuery(id+"F0.wireOp",EDGE,"E33"),sQuery(id+"F0.wireOp",EDGE,"E34")])]});
            var Q18;
            Q18=makeQuery(id+"F3.opExtrude","SWEPT_EDGE",EDGE,{"disambiguationData":[OSD([sQuery(id+"F0.wireOp",EDGE,"E29"),sQuery(id+"F0.wireOp",EDGE,"E35")])]});
            var Q19;
            Q19=makeQuery(id+"F3.opExtrude","SWEPT_EDGE",EDGE,{"disambiguationData":[OSD([sQuery(id+"F0.wireOp",EDGE,"E34"),sQuery(id+"F0.wireOp",EDGE,"E35")])]});
            var Q20;
            Q20=makeQuery(id+"F3.opExtrude","SWEPT_EDGE",EDGE,{"disambiguationData":[OSD([sQuery(id+"F0.wireOp",EDGE,"E37"),sQuery(id+"F0.wireOp",EDGE,"E38")])]});
            var Q21;
            Q21=makeQuery(id+"F3.opExtrude","SWEPT_EDGE",EDGE,{"disambiguationData":[OSD([sQuery(id+"F0.wireOp",EDGE,"E36"),sQuery(id+"F0.wireOp",EDGE,"E37")])]});
            var Q22;
            Q22=makeQuery(id+"F3.opExtrude","SWEPT_EDGE",EDGE,{"disambiguationData":[OSD([sQuery(id+"F0.wireOp",EDGE,"E31"),sQuery(id+"F0.wireOp",EDGE,"E36")])]});
            var Q23;
            Q23=makeQuery(id+"F3.opExtrude","SWEPT_EDGE",EDGE,{"disambiguationData":[OSD([sQuery(id+"F0.wireOp",EDGE,"E31"),sQuery(id+"F0.wireOp",EDGE,"E38")])]});
            fillet(context, id + "F9", {"entities" : qUnion([Q0, Q1, Q2, Q3, Q4, Q5, Q6, Q7, Q8, Q9, Q10, Q11, Q12, Q13, Q14, Q15, Q16, Q17, Q18, Q19, Q20, Q21, Q22, Q23]), "radius" : .5 * mm, "tangentPropagation" : true, "allowEdgeOverflow" : false});
        }
        {
            var Q0;
            Q0=makeQuery(id+"F1.opExtrude","SWEPT_BODY",BODY,{"disambiguationData":[OSD([sQuery(id+"F0.wireOp",EDGE,"E0"),sQuery(id+"F0.wireOp",EDGE,"E1"),sQuery(id+"F0.wireOp",EDGE,"E2"),sQuery(id+"F0.wireOp",EDGE,"E3"),sQuery(id+"F0.wireOp",EDGE,"E4"),sQuery(id+"F0.wireOp",EDGE,"E5"),sQuery(id+"F0.wireOp",EDGE,"E14"),sQuery(id+"F0.wireOp",EDGE,"E15")])]});
            var Q1;
            {var subQ0=sQuery(id+"F0.wireOp",EDGE,"E1");Q1=makeQuery(id+"F2.boolean.opBoolean","MERGE",FACE,{"derivedFrom":[makeQuery(id+"F1.opExtrude","SWEPT_FACE",FACE,{"disambiguationData":[OSD([subQ0])]}),makeQuery(id+"F2.opExtrude","SWEPT_FACE",FACE,{"disambiguationData":[OSD([subQ0])]})]});}
            mirror(context, id + "F10", {"entities" : qUnion([Q0]), "mirrorPlane" : qUnion([Q1])});
        }
        {
            var Q0;
            Q0=makeQuery(id+"F10.opPattern","COPY",BODY,{"derivedFrom":makeQuery(id+"F1.opExtrude","SWEPT_BODY",BODY,{"disambiguationData":[OSD([sQuery(id+"F0.wireOp",EDGE,"E0"),sQuery(id+"F0.wireOp",EDGE,"E1"),sQuery(id+"F0.wireOp",EDGE,"E2"),sQuery(id+"F0.wireOp",EDGE,"E3"),sQuery(id+"F0.wireOp",EDGE,"E4"),sQuery(id+"F0.wireOp",EDGE,"E5"),sQuery(id+"F0.wireOp",EDGE,"E14"),sQuery(id+"F0.wireOp",EDGE,"E15")])]}),"instanceName":"1"});
            transform(context, id + "F11", {"entities" : qUnion([Q0]), "transformType" : TransformType.TRANSLATION_3D, "dx" : 0 * mm, "dy" : -9.1 * mm, "dz" : 0 * mm, "makeCopy" : false});
        }
    });
